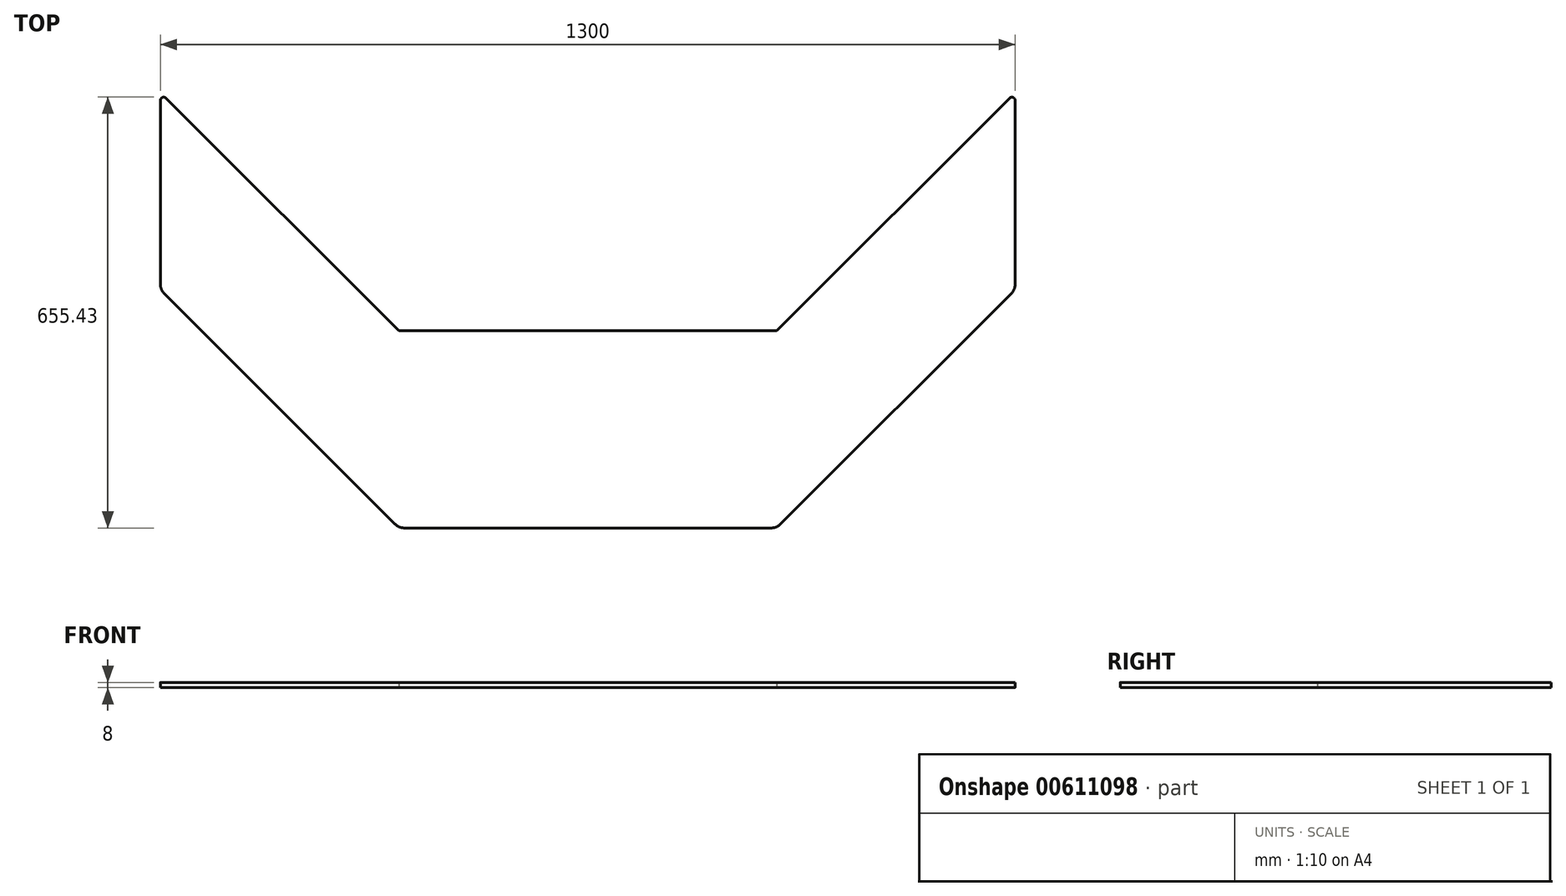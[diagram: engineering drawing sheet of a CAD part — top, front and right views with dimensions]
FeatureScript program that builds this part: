
annotation { "Feature Type Name" : "Feature", "Feature Type Description" : "" }
export const myFeature = defineFeature(function(context is Context, id is Id, definition is map)
    precondition{}
    {
        {
            var Q0;
            Q0=qCreatedBy(makeId("Top.planeOp"),FACE);
            var sketch = newSketch(context, id + "F0", { "sketchPlane" : qUnion([Q0])});
            skLineSegment(sketch, "E0", {"start": v(-287.5, 150) * mm, "end": v(287.5, 150) * mm});
            skLineSegment(sketch, "E1", {"start": v(287.5, 150) * mm, "end": v(641.46, 503.96) * mm});
            skLineSegment(sketch, "E2", {"start": v(650, 500.43) * mm, "end": v(650, 220.78) * mm});
            skLineSegment(sketch, "E3", {"start": v(279.22, -150) * mm, "end": v(-279.22, -150) * mm});
            skLineSegment(sketch, "E4", {"start": v(-650, 220.78) * mm, "end": v(-650, 500.43) * mm});
            skLineSegment(sketch, "E5", {"start": v(-641.46, 503.96) * mm, "end": v(-287.5, 150) * mm});
            skLineSegment(sketch, "E6", {"start": v(293.36, -144.14) * mm, "end": v(644.14, 206.64) * mm});
            skPoint(sketch, "E7.orphan", {"position": v(650, -150) * mm});
            skLineSegment(sketch, "E8", {"start": v(-644.14, 206.64) * mm, "end": v(-293.36, -144.14) * mm});
            skPoint(sketch, "E9.orphan", {"position": v(-650, -150) * mm});
            skLineSegment(sketch, "E10", {"start": v(-287.5, 150) * mm, "end": v(-287.5, -150) * mm, "construction": true});
            skLineSegment(sketch, "E11", {"start": v(287.5, 150) * mm, "end": v(287.5, -150) * mm, "construction": true});
            skPoint(sketch, "E12.visualSharp", {"position": v(-650, 512.5) * mm});
            skArc(sketch, "E12.filletArc", {"start": v(-641.46, 503.96) * mm, "mid": v(-646.91, 505.05) * mm, "end": v(-650, 500.43) * mm});
            skPoint(sketch, "E13.visualSharp", {"position": v(-650, 212.5) * mm});
            skArc(sketch, "E13.filletArc", {"start": v(-650, 220.78) * mm, "mid": v(-648.48, 213.13) * mm, "end": v(-644.14, 206.64) * mm});
            skPoint(sketch, "E14.visualSharp", {"position": v(-287.5, -150) * mm});
            skArc(sketch, "E14.filletArc", {"start": v(-293.36, -144.14) * mm, "mid": v(-286.87, -148.48) * mm, "end": v(-279.22, -150) * mm});
            skPoint(sketch, "E15.visualSharp", {"position": v(287.5, -150) * mm});
            skArc(sketch, "E15.filletArc", {"start": v(279.22, -150) * mm, "mid": v(286.87, -148.48) * mm, "end": v(293.36, -144.14) * mm});
            skPoint(sketch, "E16.visualSharp", {"position": v(650, 212.5) * mm});
            skArc(sketch, "E16.filletArc", {"start": v(644.14, 206.64) * mm, "mid": v(648.48, 213.13) * mm, "end": v(650, 220.78) * mm});
            skPoint(sketch, "E17.visualSharp", {"position": v(287.5, 150) * mm});
            skPoint(sketch, "E18.visualSharp", {"position": v(650, 512.5) * mm});
            skArc(sketch, "E18.filletArc", {"start": v(650, 500.43) * mm, "mid": v(646.91, 505.05) * mm, "end": v(641.46, 503.96) * mm});
            skSolve(sketch);
        }
        {
            var Q0;
            Q0=qSketchRegion(id+"F0",true);
            extrude(context, id + "F1", {"entities" : qUnion([Q0]), "depth" : 8 * mm, "offsetDistance" : 25 * mm});
        }
    });
